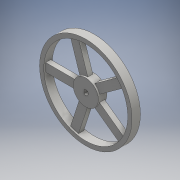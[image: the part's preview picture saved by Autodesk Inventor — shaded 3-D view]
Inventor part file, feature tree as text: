
AUTODESK INVENTOR PART (.ipt)
format: ipt  version: 2016 (Build 200138000, 138)  size: 145,920 bytes
history: native  units: mm
features: extrude x2, sketch x2, other x1, pattern_circular x1
ambient origin geometry x8: Origin, YZ Plane, XZ Plane, XY Plane, X Axis, Y Axis, Z Axis, Center Point
bodies: Body1 (feature_tree)
feature tree (6):
  other  "Sólido1"
  extrude  "Extrusión1"  Depth=50.0mm
  extrude  "Extrusión2"  Depth=3.0mm
  pattern_circular  "Patrón circular1"  [2 undecoded]
  sketch  "Boceto1"  dims[d0=55.0mm d1=50.0mm]
  sketch  "Boceto2"  dims[d2=15.0mm d3=3.0mm d6=1.0mm d7=5.0mm d8=0.0mm d9=15.0mm d10=50.0mm d12=2.5mm d13=3.0mm d14=0.0mm d15=50.0mm d16=360.0deg]
note: 2 required parameter values undecoded (feature->parameter linkage not recoverable at this tier; creation-order binding heuristic only, values carry confidence <= 0.55)
